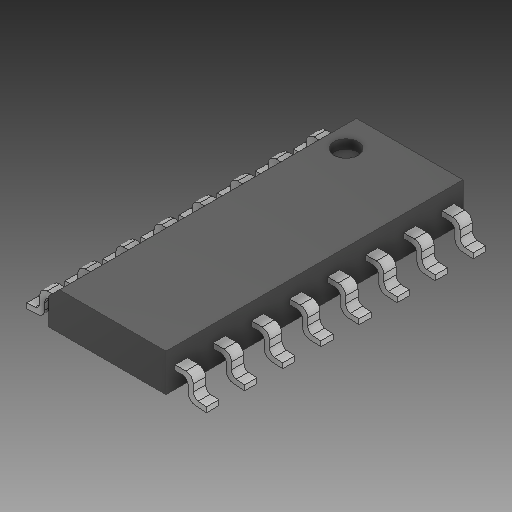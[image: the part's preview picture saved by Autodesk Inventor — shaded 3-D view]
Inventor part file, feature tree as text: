
AUTODESK INVENTOR PART (.ipt)
format: ipt  version: 2020 (Build 240168000, 168)  size: 249,344 bytes
history: native  units: mm
features: other x1, chamfer x1
ambient origin geometry x8: Origin, YZ Plane, XZ Plane, XY Plane, X Axis, Y Axis, Z Axis, Center Point
bodies: Body1 (feature_tree)
feature tree (2):
  other  "Твердое тело1"
  chamfer  "Chamfer1"  [1 undecoded]
note: 1 required parameter value undecoded (feature->parameter linkage not recoverable at this tier; creation-order binding heuristic only, values carry confidence <= 0.55)
